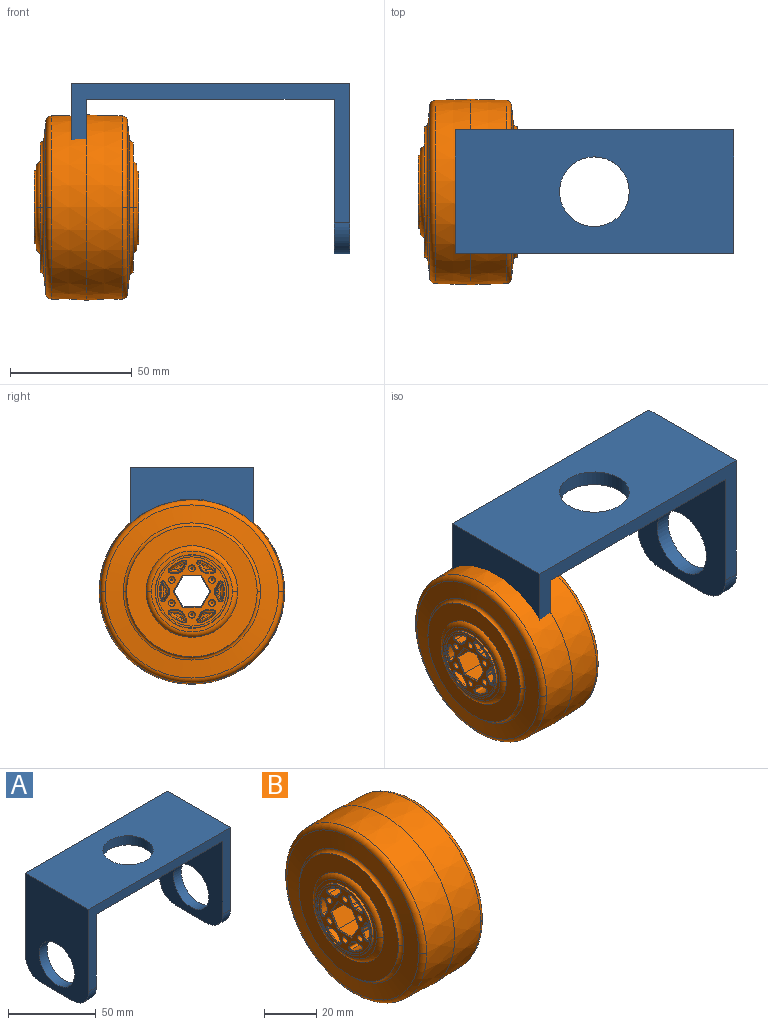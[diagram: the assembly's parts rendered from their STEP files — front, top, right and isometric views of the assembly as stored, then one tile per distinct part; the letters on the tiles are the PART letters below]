
ASSEMBLY  parts=2 mates=1
PART A: 17 faces, bbox 114.3x50.8x69.9 mm
  f0: plane 25.4x6.35mm, normal (0,0,-1), area 161.3mm2, adj f1,f7,f13,f15
  f1: plane 69.85x50.8mm, normal (1,0,0), area 2837.9mm2, adj f0,f2,f8,f9,f10,f13,f15
  f2: plane 114.3x50.8mm, normal (0,0,1), area 5165.1mm2, adj f1,f3,f8,f9,f16
  f3: plane 69.85x50.8mm, normal (-1,0,0), area 2837.9mm2, adj f2,f4,f8,f9,f11,f12,f14
  f4: plane 25.4x6.35mm, normal (0,0,-1), area 161.3mm2, adj f3,f5,f12,f14
  f5: plane 63.5x50.8mm, normal (1,0,0), area 2515.3mm2, adj f4,f6,f8,f9,f11,f12,f14
  f6: plane 101.6x50.8mm, normal (0,0,-1), area 4520mm2, adj f5,f7,f8,f9,f16
  f7: plane 63.5x50.8mm, normal (-1,0,0), area 2515.3mm2, adj f0,f6,f8,f9,f10,f13,f15
  f8: plane 114.3x57.15mm, normal (0,-1,0), area 1371mm2, adj f1,f2,f3,f5,f6,f7,f14,f15
  f9: plane 114.3x57.15mm, normal (0,1,0), area 1371mm2, adj f1,f2,f3,f5,f6,f7,f12,f13
  f10: cylinder r=14.29mm len=28.58mm, axis (1,0,0), area 570mm2, adj f1,f7
  f11: cylinder r=14.29mm len=28.58mm, axis (1,0,0), area 570mm2, adj f3,f5
  f12: cylinder r=12.7mm len=12.7mm, axis (1,0,0), area 126.7mm2, adj f3,f4,f5,f9
  f13: cylinder r=12.7mm len=12.7mm, axis (1,0,0), area 126.7mm2, adj f0,f1,f7,f9
  f14: cylinder r=12.7mm len=12.7mm, axis (-1,0,0), area 126.7mm2, adj f3,f4,f5,f8
  f15: cylinder r=12.7mm len=12.7mm, axis (-1,0,0), area 126.7mm2, adj f0,f1,f7,f8
  f16: cylinder r=14.29mm len=28.58mm, axis (0,0,1), area 570mm2, adj f2,f6
PART B: 338 faces, bbox 44.4x82.9x82.9 mm
  f0: torus R=35.31mm, axis (-1,0,0), area 378.6mm2, adj f38,f40,f52
  f1: torus R=35.31mm, axis (-1,0,0), area 378.6mm2, adj f39,f41,f53
  f2: torus R=28.32mm, axis (-1,0,0), area 191.5mm2, adj f40,f48,f54
  f3: torus R=28.32mm, axis (-1,0,0), area 191.5mm2, adj f41,f51,f55
  f4: torus R=16.62mm, axis (-1,0,0), area 161.8mm2, adj f49,f50,f51
  f5: torus R=16.62mm, axis (-1,0,0), area 161.8mm2, adj f46,f47,f48
  f6: cone r=14.2mm half-angle=0.5deg, axis (1,0,0), area 26.8mm2, adj f56,f57
  f7: cylinder r=1.38mm len=18.65mm, axis (1,0,0), area 161.1mm2, adj f14,f57
  f8: cylinder r=1.38mm len=18.65mm, axis (1,0,0), area 161.1mm2, adj f15,f57
  f9: cylinder r=1.38mm len=18.65mm, axis (1,0,0), area 161.1mm2, adj f16,f57
  f10: cylinder r=1.38mm len=18.65mm, axis (1,0,0), area 161.1mm2, adj f17,f57
  f11: cylinder r=1.38mm len=18.65mm, axis (1,0,0), area 161.1mm2, adj f18,f57
  f12: cylinder r=1.38mm len=18.65mm, axis (1,0,0), area 161.1mm2, adj f19,f57
  f13: cone r=13.01mm half-angle=1.5deg, axis (1,0,0), area 128.2mm2, adj f59,f112,f113,f147
  f14: torus R=0.38mm, axis (1,0,0), area 10mm2, adj f7,f177
  f15: torus R=0.38mm, axis (1,0,0), area 10mm2, adj f8,f178
  f16: torus R=0.38mm, axis (1,0,0), area 10mm2, adj f9,f179
  f17: torus R=0.38mm, axis (1,0,0), area 10mm2, adj f10,f180
  f18: torus R=0.38mm, axis (1,0,0), area 10mm2, adj f11,f181
  f19: torus R=0.38mm, axis (1,0,0), area 10mm2, adj f12,f182
  f20: cone r=10.06mm half-angle=1.5deg, axis (-1,0,0), area 23.4mm2, adj f87,f163,f166,f200
  f21: cone r=14.2mm half-angle=0.5deg, axis (-1,0,0), area 26.8mm2, adj f189,f207
  f22: cylinder r=1.38mm len=18.65mm, axis (-1,0,0), area 161.1mm2, adj f29,f207
  f23: cylinder r=1.38mm len=18.65mm, axis (-1,0,0), area 161.1mm2, adj f30,f207
  f24: cylinder r=1.38mm len=18.65mm, axis (-1,0,0), area 161.1mm2, adj f31,f207
  f25: cylinder r=1.38mm len=18.65mm, axis (-1,0,0), area 161.1mm2, adj f32,f207
  f26: cylinder r=1.38mm len=18.65mm, axis (-1,0,0), area 161.1mm2, adj f33,f207
  f27: cylinder r=1.38mm len=18.65mm, axis (-1,0,0), area 161.1mm2, adj f34,f207
  f28: cone r=13.01mm half-angle=1.5deg, axis (-1,0,0), area 128.2mm2, adj f249,f281,f282,f310
  f29: torus R=0.38mm, axis (-1,0,0), area 10mm2, adj f22,f315
  f30: torus R=0.38mm, axis (-1,0,0), area 10mm2, adj f23,f316
  f31: torus R=0.38mm, axis (-1,0,0), area 10mm2, adj f24,f317
  f32: torus R=0.38mm, axis (-1,0,0), area 10mm2, adj f25,f318
  f33: torus R=0.38mm, axis (-1,0,0), area 10mm2, adj f26,f319
  f34: torus R=0.38mm, axis (-1,0,0), area 10mm2, adj f27,f320
  f35: cone r=10.06mm half-angle=1.5deg, axis (1,0,0), area 23.4mm2, adj f231,f295,f298,f327
  f36: cone r=15.17mm half-angle=0.5deg, axis (-1,0,0), area 316mm2, adj f44,f56
  f37: cone r=15.17mm half-angle=0.5deg, axis (1,0,0), area 304.2mm2, adj f45,f189
  f38: cone r=38.1mm half-angle=2deg, axis (-1,0,0), area 3465.4mm2, adj f0,f39,f52
  f39: cone r=38.1mm half-angle=2deg, axis (1,0,0), area 3465.4mm2, adj f1,f38,f53
  f40: cone r=35.55mm half-angle=84deg, axis (-1,0,0), area 1486mm2, adj f0,f2,f52,f54
  f41: cone r=35.55mm half-angle=84deg, axis (1,0,0), area 1486mm2, adj f1,f3,f53,f55
  f42: cylinder r=15.11mm len=30.21mm, axis (-1,0,0), area 230.8mm2, adj f45,f49
  f43: cylinder r=15.11mm len=30.21mm, axis (-1,0,0), area 243mm2, adj f44,f46
  f44: cone r=31.03mm half-angle=77.6deg, axis (-1,0,0), area 7.8mm2, adj f36,f43
  f45: cone r=13.82mm half-angle=79.3deg, axis (1,0,0), area 7.8mm2, adj f37,f42
  f46: plane 33.24x33.24mm, normal (1,0,0), area 150.8mm2, adj f5,f43,f47
  f47: torus R=16.62mm, axis (-1,0,0), area 161.8mm2, adj f5,f46,f48
  f48: plane 53.59x53.59mm, normal (1,0,0), area 1146mm2, adj f2,f5,f47,f54
  f49: plane 33.24x33.24mm, normal (-1,0,0), area 150.8mm2, adj f4,f42,f50
  f50: torus R=16.62mm, axis (-1,0,0), area 161.8mm2, adj f4,f49,f51
  f51: plane 53.59x53.59mm, normal (-1,0,0), area 1146mm2, adj f3,f4,f50,f55
  f52: torus R=35.31mm, axis (-1,0,0), area 378.6mm2, adj f0,f38,f40
  f53: torus R=35.31mm, axis (-1,0,0), area 378.6mm2, adj f1,f39,f41
  f54: torus R=28.32mm, axis (-1,0,0), area 191.5mm2, adj f2,f40,f48
  f55: torus R=28.32mm, axis (-1,0,0), area 191.5mm2, adj f3,f41,f51
  f56: plane 29.99x29.99mm, normal (1,0,0), area 72.9mm2, adj f6,f36
  f57: plane 28.52x28.52mm, normal (1,0,0), area 288.3mm2, adj f6,f7,f8,f9,f10,f11,f12,f58
  f58: bspline ~2.05x0.93mm, area 1mm2, adj f57,f59,f65,f112
  f59: torus R=13.31mm, axis (1,0,0), area 3.3mm2, adj f13,f57,f58,f60
  f60: bspline ~2.04x0.95mm, area 1mm2, adj f57,f59,f61,f113
  f61: cylinder r=0.3mm len=2.75mm, axis (0,0.5,0.87), area 1.4mm2, adj f57,f60,f62,f114
  f62: bspline ~0.74x0.49mm, area 0.3mm2, adj f57,f61,f63,f148
  f63: torus R=9.28mm, axis (1,0,0), area 0.6mm2, adj f57,f62,f64,f191
  f64: bspline ~0.72x0.49mm, area 0.3mm2, adj f57,f63,f65,f151
  f65: cylinder r=0.3mm len=2.75mm, axis (0,-0.5,0.87), area 1.4mm2, adj f57,f58,f64,f115
  f66: bspline ~1.72x1.42mm, area 1mm2, adj f57,f67,f73,f116
  f67: torus R=13.31mm, axis (1,0,0), area 3.3mm2, adj f57,f66,f68,f117
  f68: bspline ~1.92x1.14mm, area 1mm2, adj f57,f67,f69,f118
  f69: cylinder r=0.3mm len=3mm, axis (0,1,0), area 1.4mm2, adj f57,f68,f70,f119
  f70: bspline ~0.73x0.52mm, area 0.3mm2, adj f57,f69,f71,f153
  f71: torus R=9.28mm, axis (1,0,0), area 0.6mm2, adj f57,f70,f72,f194
  f72: bspline ~0.7x0.68mm, area 0.3mm2, adj f57,f71,f73,f156
  f73: cylinder r=0.3mm len=2.75mm, axis (0,0.5,0.87), area 1.4mm2, adj f57,f66,f72,f120
  f74: bspline ~1.9x1.15mm, area 1mm2, adj f57,f75,f81,f121
  f75: torus R=13.31mm, axis (1,0,0), area 3.3mm2, adj f57,f74,f76,f122
  f76: bspline ~1.69x1.45mm, area 1mm2, adj f57,f75,f77,f123
  f77: cylinder r=0.3mm len=2.75mm, axis (0,0.5,-0.87), area 1.4mm2, adj f57,f76,f78,f124
  f78: bspline ~0.7x0.68mm, area 0.3mm2, adj f57,f77,f79,f158
  f79: torus R=9.28mm, axis (1,0,0), area 0.6mm2, adj f57,f78,f80,f197
  f80: bspline ~0.73x0.51mm, area 0.3mm2, adj f57,f79,f81,f161
  f81: cylinder r=0.3mm len=3mm, axis (0,1,0), area 1.4mm2, adj f57,f74,f80,f125
  f82: bspline ~2.05x0.93mm, area 1mm2, adj f57,f83,f89,f126
  f83: torus R=13.31mm, axis (1,0,0), area 3.3mm2, adj f57,f82,f84,f127
  f84: bspline ~2.04x0.95mm, area 1mm2, adj f57,f83,f85,f128
  f85: cylinder r=0.3mm len=2.75mm, axis (0,-0.5,-0.87), area 1.4mm2, adj f57,f84,f86,f129
  f86: bspline ~0.74x0.49mm, area 0.3mm2, adj f57,f85,f87,f163
  f87: torus R=9.28mm, axis (1,0,0), area 0.6mm2, adj f20,f57,f86,f88
  f88: bspline ~0.72x0.49mm, area 0.3mm2, adj f57,f87,f89,f166
  f89: cylinder r=0.3mm len=2.75mm, axis (0,0.5,-0.87), area 1.4mm2, adj f57,f82,f88,f130
  f90: bspline ~1.72x1.42mm, area 1mm2, adj f57,f91,f97,f131
  f91: torus R=13.31mm, axis (1,0,0), area 3.3mm2, adj f57,f90,f92,f132
  f92: bspline ~1.92x1.14mm, area 1mm2, adj f57,f91,f93,f133
  f93: cylinder r=0.3mm len=3mm, axis (0,-1,0), area 1.4mm2, adj f57,f92,f94,f134
  f94: bspline ~0.73x0.52mm, area 0.3mm2, adj f57,f93,f95,f168
  f95: torus R=9.28mm, axis (1,0,0), area 0.6mm2, adj f57,f94,f96,f202
  f96: bspline ~0.7x0.68mm, area 0.3mm2, adj f57,f95,f97,f171
  f97: cylinder r=0.3mm len=2.75mm, axis (0,-0.5,-0.87), area 1.4mm2, adj f57,f90,f96,f135
  f98: bspline ~1.9x1.15mm, area 1mm2, adj f57,f99,f105,f136
  f99: torus R=13.31mm, axis (1,0,0), area 3.3mm2, adj f57,f98,f100,f137
  f100: bspline ~1.69x1.45mm, area 1mm2, adj f57,f99,f101,f138
  f101: cylinder r=0.3mm len=2.75mm, axis (0,-0.5,0.87), area 1.4mm2, adj f57,f100,f102,f139
  f102: bspline ~0.7x0.68mm, area 0.3mm2, adj f57,f101,f103,f173
  f103: torus R=9.28mm, axis (1,0,0), area 0.6mm2, adj f57,f102,f104,f205
  f104: bspline ~0.73x0.51mm, area 0.3mm2, adj f57,f103,f105,f176
  f105: cylinder r=0.3mm len=3mm, axis (0,-1,0), area 1.4mm2, adj f57,f98,f104,f140
  f106: plane 6.66x4.02mm, normal (0.71,0.61,0.35), area 3.2mm2, adj f57,f107,f111,f141
  f107: plane 7.69x0.3mm, normal (0.71,0,0.71), area 3.2mm2, adj f57,f106,f108,f142
  f108: plane 6.66x4.02mm, normal (0.71,-0.61,0.35), area 3.2mm2, adj f57,f107,f109,f143
  f109: plane 6.66x4.02mm, normal (0.71,-0.61,-0.35), area 3.2mm2, adj f57,f108,f110,f144
  f110: plane 7.69x0.3mm, normal (0.71,0,-0.71), area 3.2mm2, adj f57,f109,f111,f145
  f111: plane 6.66x4.02mm, normal (0.71,0.61,-0.35), area 3.2mm2, adj f57,f106,f110,f146
  f112: revolved ~19.11x1.39mm, area 22.6mm2, adj f13,f58,f115,f147,f150
  f113: revolved ~19.11x1.39mm, area 22.6mm2, adj f13,f60,f114,f147,f149
  f114: plane 18.67x2.84mm, normal (0.03,0.87,-0.5), area 56mm2, adj f61,f113,f148,f149
  f115: plane 18.67x2.84mm, normal (0.03,0.87,0.5), area 56mm2, adj f65,f112,f150,f151
  f116: revolved ~19.11x1.14mm, area 22.6mm2, adj f66,f117,f120,f152,f155
  f117: cone r=13.01mm half-angle=1.5deg, axis (1,0,0), area 128.2mm2, adj f67,f116,f118,f152
  f118: revolved ~19.11x1.29mm, area 22.6mm2, adj f68,f117,f119,f152,f154
  f119: plane 18.67x3mm, normal (0.03,0,-1), area 56mm2, adj f69,f118,f153,f154
  f120: plane 18.67x2.84mm, normal (0.03,0.87,-0.5), area 56mm2, adj f73,f116,f155,f156
  f121: revolved ~19.11x1.29mm, area 22.6mm2, adj f74,f122,f125,f157,f160
  f122: cone r=13.01mm half-angle=1.5deg, axis (1,0,0), area 128.2mm2, adj f75,f121,f123,f157
  f123: revolved ~19.11x1.14mm, area 22.6mm2, adj f76,f122,f124,f157,f159
  f124: plane 18.67x2.84mm, normal (0.03,-0.87,-0.5), area 56mm2, adj f77,f123,f158,f159
  f125: plane 18.67x3mm, normal (0.03,0,-1), area 56mm2, adj f81,f121,f160,f161
  f126: revolved ~19.11x1.39mm, area 22.6mm2, adj f82,f127,f130,f162,f165
  f127: cone r=13.01mm half-angle=1.5deg, axis (1,0,0), area 128.2mm2, adj f83,f126,f128,f162
  f128: revolved ~19.11x1.39mm, area 22.6mm2, adj f84,f127,f129,f162,f164
  f129: plane 18.67x2.84mm, normal (0.03,-0.87,0.5), area 56mm2, adj f85,f128,f163,f164
  f130: plane 18.67x2.84mm, normal (0.03,-0.87,-0.5), area 56mm2, adj f89,f126,f165,f166
  f131: revolved ~19.11x1.14mm, area 22.6mm2, adj f90,f132,f135,f167,f170
  f132: cone r=13.01mm half-angle=1.5deg, axis (1,0,0), area 128.2mm2, adj f91,f131,f133,f167
  f133: revolved ~19.11x1.29mm, area 22.6mm2, adj f92,f132,f134,f167,f169
  f134: plane 18.67x3mm, normal (0.03,0,1), area 56mm2, adj f93,f133,f168,f169
  f135: plane 18.67x2.84mm, normal (0.03,-0.87,0.5), area 56mm2, adj f97,f131,f170,f171
  f136: revolved ~19.11x1.29mm, area 22.6mm2, adj f98,f137,f140,f172,f175
  f137: cone r=13.01mm half-angle=1.5deg, axis (1,0,0), area 128.2mm2, adj f99,f136,f138,f172
  f138: revolved ~19.11x1.14mm, area 22.6mm2, adj f100,f137,f139,f172,f174
  f139: plane 18.67x2.84mm, normal (0.03,0.87,0.5), area 56mm2, adj f101,f138,f173,f174
  f140: plane 18.67x3mm, normal (0.03,0,1), area 56mm2, adj f105,f136,f175,f176
  f141: plane 41.69x6.36mm, normal (0,0.87,0.5), area 306.3mm2, adj f106,f142,f146,f183
  f142: plane 41.69x7.35mm, normal (0,0,1), area 306.3mm2, adj f107,f141,f143,f184
  f143: plane 41.69x6.36mm, normal (0,-0.87,0.5), area 306.3mm2, adj f108,f142,f144,f185
  f144: plane 41.69x6.36mm, normal (0,-0.87,-0.5), area 306.3mm2, adj f109,f143,f145,f186
  f145: plane 41.69x7.35mm, normal (0,0,-1), area 306.3mm2, adj f110,f144,f146,f187
  f146: plane 41.69x6.36mm, normal (0,0.87,-0.5), area 306.3mm2, adj f111,f141,f145,f188
  f147: torus R=11.82mm, axis (1,0,0), area 6.7mm2, adj f13,f112,f113,f149,f150,f190
  f148: bspline ~19.55x0.57mm, area 5.6mm2, adj f62,f114,f149,f191,f192
  f149: cylinder r=0.7mm len=3.22mm, axis (0,0.5,0.87), area 3.1mm2, adj f113,f114,f147,f148,f190,f192
  f150: cylinder r=0.7mm len=3.22mm, axis (0,-0.5,0.87), area 3.1mm2, adj f112,f115,f147,f151,f190,f192
  f151: bspline ~19.55x0.57mm, area 5.6mm2, adj f64,f115,f150,f191,f192
  f152: torus R=11.82mm, axis (1,0,0), area 6.7mm2, adj f116,f117,f118,f154,f155,f193
  f153: bspline ~19.55x0.57mm, area 5.6mm2, adj f70,f119,f154,f194,f195
  f154: cylinder r=0.7mm len=3.31mm, axis (0,1,0), area 3.1mm2, adj f118,f119,f152,f153,f193,f195
  f155: cylinder r=0.7mm len=3.22mm, axis (0,0.5,0.87), area 3.1mm2, adj f116,f120,f152,f156,f193,f195
  f156: bspline ~19.55x0.59mm, area 5.6mm2, adj f72,f120,f155,f194,f195
  f157: torus R=11.82mm, axis (1,0,0), area 6.7mm2, adj f121,f122,f123,f159,f160,f196
  f158: bspline ~19.55x0.59mm, area 5.6mm2, adj f78,f124,f159,f197,f198
  f159: cylinder r=0.7mm len=3.22mm, axis (0,0.5,-0.87), area 3.1mm2, adj f123,f124,f157,f158,f196,f198
  f160: cylinder r=0.7mm len=3.31mm, axis (0,1,0), area 3.1mm2, adj f121,f125,f157,f161,f196,f198
  f161: bspline ~19.55x0.57mm, area 5.6mm2, adj f80,f125,f160,f197,f198
  f162: torus R=11.82mm, axis (1,0,0), area 6.7mm2, adj f126,f127,f128,f164,f165,f199
  f163: bspline ~19.55x0.57mm, area 5.6mm2, adj f20,f86,f129,f164,f200
  f164: cylinder r=0.7mm len=3.22mm, axis (0,-0.5,-0.87), area 3.1mm2, adj f128,f129,f162,f163,f199,f200
  f165: cylinder r=0.7mm len=3.22mm, axis (0,0.5,-0.87), area 3.1mm2, adj f126,f130,f162,f166,f199,f200
  f166: bspline ~19.55x0.57mm, area 5.6mm2, adj f20,f88,f130,f165,f200
  f167: torus R=11.82mm, axis (1,0,0), area 6.7mm2, adj f131,f132,f133,f169,f170,f201
  f168: bspline ~19.55x0.57mm, area 5.6mm2, adj f94,f134,f169,f202,f203
  f169: cylinder r=0.7mm len=3.31mm, axis (0,-1,0), area 3.1mm2, adj f133,f134,f167,f168,f201,f203
  f170: cylinder r=0.7mm len=3.22mm, axis (0,-0.5,-0.87), area 3.1mm2, adj f131,f135,f167,f171,f201,f203
  f171: bspline ~19.55x0.59mm, area 5.6mm2, adj f96,f135,f170,f202,f203
  f172: torus R=11.82mm, axis (1,0,0), area 6.7mm2, adj f136,f137,f138,f174,f175,f204
  f173: bspline ~19.55x0.59mm, area 5.6mm2, adj f102,f139,f174,f205,f206
  f174: cylinder r=0.7mm len=3.22mm, axis (0,-0.5,0.87), area 3.1mm2, adj f138,f139,f172,f173,f204,f206
  f175: cylinder r=0.7mm len=3.31mm, axis (0,-1,0), area 3.1mm2, adj f136,f140,f172,f176,f204,f206
  f176: bspline ~19.55x0.57mm, area 5.6mm2, adj f104,f140,f175,f205,f206
  f177: plane 0.75x0.75mm, normal (1,0,0), area 0.4mm2, adj f14
  f178: plane 0.75x0.75mm, normal (1,0,0), area 0.4mm2, adj f15
  f179: plane 0.75x0.75mm, normal (1,0,0), area 0.4mm2, adj f16
  f180: plane 0.75x0.75mm, normal (1,0,0), area 0.4mm2, adj f17
  f181: plane 0.75x0.75mm, normal (1,0,0), area 0.4mm2, adj f18
  f182: plane 0.75x0.75mm, normal (1,0,0), area 0.4mm2, adj f19
  f183: plane 6.66x4.02mm, normal (-0.71,0.61,0.35), area 3.2mm2, adj f141,f184,f188,f207
  f184: plane 7.69x0.3mm, normal (-0.71,0,0.71), area 3.2mm2, adj f142,f183,f185,f207
  f185: plane 6.66x4.02mm, normal (-0.71,-0.61,0.35), area 3.2mm2, adj f143,f184,f186,f207
  f186: plane 6.66x4.02mm, normal (-0.71,-0.61,-0.35), area 3.2mm2, adj f144,f185,f187,f207
  f187: plane 7.69x0.3mm, normal (-0.71,0,-0.71), area 3.2mm2, adj f145,f186,f188,f207
  f188: plane 6.66x4.02mm, normal (-0.71,0.61,-0.35), area 3.2mm2, adj f146,f183,f187,f207
  f189: plane 29.99x29.99mm, normal (-1,0,0), area 72.9mm2, adj f21,f37
  f190: plane 4.17x1.07mm, normal (1,0,0), area 2.8mm2, adj f147,f149,f150,f192
  f191: cone r=10.06mm half-angle=1.5deg, axis (-1,0,0), area 23.4mm2, adj f63,f148,f151,f192
  f192: torus R=10.76mm, axis (1,0,0), area 1.4mm2, adj f148,f149,f150,f151,f190,f191
  f193: plane 3.61x2.08mm, normal (1,0,0), area 2.8mm2, adj f152,f154,f155,f195
  f194: cone r=10.06mm half-angle=1.5deg, axis (-1,0,0), area 23.4mm2, adj f71,f153,f156,f195
  f195: torus R=10.76mm, axis (1,0,0), area 1.4mm2, adj f153,f154,f155,f156,f193,f194
  f196: plane 3.61x2.08mm, normal (1,0,0), area 2.8mm2, adj f157,f159,f160,f198
  f197: cone r=10.06mm half-angle=1.5deg, axis (-1,0,0), area 23.4mm2, adj f79,f158,f161,f198
  f198: torus R=10.76mm, axis (1,0,0), area 1.4mm2, adj f158,f159,f160,f161,f196,f197
  f199: plane 4.17x1.07mm, normal (1,0,0), area 2.8mm2, adj f162,f164,f165,f200
  f200: torus R=10.76mm, axis (1,0,0), area 1.4mm2, adj f20,f163,f164,f165,f166,f199
  f201: plane 3.61x2.08mm, normal (1,0,0), area 2.8mm2, adj f167,f169,f170,f203
  f202: cone r=10.06mm half-angle=1.5deg, axis (-1,0,0), area 23.4mm2, adj f95,f168,f171,f203
  f203: torus R=10.76mm, axis (1,0,0), area 1.4mm2, adj f168,f169,f170,f171,f201,f202
  f204: plane 3.61x2.08mm, normal (1,0,0), area 2.8mm2, adj f172,f174,f175,f206
  f205: cone r=10.06mm half-angle=1.5deg, axis (-1,0,0), area 23.4mm2, adj f103,f173,f176,f206
  f206: torus R=10.76mm, axis (1,0,0), area 1.4mm2, adj f173,f174,f175,f176,f204,f205
  f207: plane 28.49x28.49mm, normal (-1,0,0), area 288.3mm2, adj f21,f22,f23,f24,f25,f26,f27,f183
  f208: bspline ~0.68x0.68mm, area 0.3mm2, adj f207,f209,f215,f285
  f209: cylinder r=0.3mm len=2.75mm, axis (0,-0.5,0.87), area 1.4mm2, adj f207,f208,f210,f256
  f210: bspline ~1.72x1.42mm, area 1.1mm2, adj f207,f209,f211,f257
  f211: torus R=13.31mm, axis (-1,0,0), area 3.3mm2, adj f207,f210,f212,f258
  f212: bspline ~1.92x1.15mm, area 1.1mm2, adj f207,f211,f213,f259
  f213: cylinder r=0.3mm len=3mm, axis (0,-1,0), area 1.4mm2, adj f207,f212,f214,f260
  f214: bspline ~0.69x0.51mm, area 0.3mm2, adj f207,f213,f215,f288
  f215: torus R=9.28mm, axis (-1,0,0), area 0.6mm2, adj f207,f208,f214,f321
  f216: bspline ~0.71x0.52mm, area 0.3mm2, adj f207,f217,f223,f290
  f217: cylinder r=0.3mm len=3mm, axis (0,-1,0), area 1.4mm2, adj f207,f216,f218,f261
  f218: bspline ~1.91x1.18mm, area 1.1mm2, adj f207,f217,f219,f262
  f219: torus R=13.31mm, axis (-1,0,0), area 3.3mm2, adj f207,f218,f220,f263
  f220: bspline ~1.69x1.45mm, area 1.1mm2, adj f207,f219,f221,f264
  f221: cylinder r=0.3mm len=2.75mm, axis (0,-0.5,-0.87), area 1.4mm2, adj f207,f220,f222,f265
  f222: bspline ~0.7x0.68mm, area 0.3mm2, adj f207,f221,f223,f293
  f223: torus R=9.28mm, axis (-1,0,0), area 0.6mm2, adj f207,f216,f222,f324
  f224: bspline ~0.72x0.49mm, area 0.3mm2, adj f207,f225,f231,f295
  f225: cylinder r=0.3mm len=2.75mm, axis (0,-0.5,-0.87), area 1.4mm2, adj f207,f224,f226,f266
  f226: bspline ~2.06x0.94mm, area 1.1mm2, adj f207,f225,f227,f267
  f227: torus R=13.31mm, axis (-1,0,0), area 3.3mm2, adj f207,f226,f228,f268
  f228: bspline ~2.05x0.95mm, area 1.1mm2, adj f207,f227,f229,f269
  f229: cylinder r=0.3mm len=2.75mm, axis (0,0.5,-0.87), area 1.4mm2, adj f207,f228,f230,f270
  f230: bspline ~0.7x0.48mm, area 0.3mm2, adj f207,f229,f231,f298
  f231: torus R=9.28mm, axis (-1,0,0), area 0.6mm2, adj f35,f207,f224,f230
  f232: bspline ~0.69x0.51mm, area 0.3mm2, adj f207,f233,f239,f303
  f233: torus R=9.28mm, axis (-1,0,0), area 0.6mm2, adj f207,f232,f234,f329
  f234: bspline ~0.68x0.68mm, area 0.3mm2, adj f207,f233,f235,f300
  f235: cylinder r=0.3mm len=2.75mm, axis (0,0.5,-0.87), area 1.4mm2, adj f207,f234,f236,f271
  f236: bspline ~1.72x1.42mm, area 1.1mm2, adj f207,f235,f237,f272
  f237: torus R=13.31mm, axis (-1,0,0), area 3.3mm2, adj f207,f236,f238,f273
  f238: bspline ~1.92x1.15mm, area 1.1mm2, adj f207,f237,f239,f274
  f239: cylinder r=0.3mm len=3mm, axis (0,1,0), area 1.4mm2, adj f207,f232,f238,f275
  f240: bspline ~0.71x0.52mm, area 0.3mm2, adj f207,f241,f247,f305
  f241: cylinder r=0.3mm len=3mm, axis (0,1,0), area 1.4mm2, adj f207,f240,f242,f276
  f242: bspline ~1.91x1.18mm, area 1.1mm2, adj f207,f241,f243,f277
  f243: torus R=13.31mm, axis (-1,0,0), area 3.3mm2, adj f207,f242,f244,f278
  f244: bspline ~1.69x1.45mm, area 1.1mm2, adj f207,f243,f245,f279
  f245: cylinder r=0.3mm len=2.75mm, axis (0,0.5,0.87), area 1.4mm2, adj f207,f244,f246,f280
  f246: bspline ~0.7x0.68mm, area 0.3mm2, adj f207,f245,f247,f308
  f247: torus R=9.28mm, axis (-1,0,0), area 0.6mm2, adj f207,f240,f246,f332
  f248: bspline ~2.06x0.94mm, area 1.1mm2, adj f207,f249,f255,f281
  f249: torus R=13.31mm, axis (-1,0,0), area 3.3mm2, adj f28,f207,f248,f250
  f250: bspline ~2.05x0.95mm, area 1.1mm2, adj f207,f249,f251,f282
  f251: cylinder r=0.3mm len=2.75mm, axis (0,-0.5,0.87), area 1.4mm2, adj f207,f250,f252,f283
  f252: bspline ~0.7x0.48mm, area 0.3mm2, adj f207,f251,f253,f311
  f253: torus R=9.28mm, axis (-1,0,0), area 0.6mm2, adj f207,f252,f254,f337
  f254: bspline ~0.72x0.49mm, area 0.3mm2, adj f207,f253,f255,f313
  f255: cylinder r=0.3mm len=2.75mm, axis (0,0.5,0.87), area 1.4mm2, adj f207,f248,f254,f284
  f256: plane 18.67x2.84mm, normal (-0.03,-0.87,-0.5), area 56mm2, adj f209,f257,f285,f286
  f257: revolved ~19.11x1.13mm, area 22.6mm2, adj f210,f256,f258,f286,f287
  f258: cone r=13.01mm half-angle=1.5deg, axis (-1,0,0), area 128.2mm2, adj f211,f257,f259,f287
  f259: revolved ~19.11x1.51mm, area 52.8mm2, adj f212,f258,f260,f287,f289
  f260: plane 20.17x4.5mm, normal (-0.03,0,-1), area 56mm2, adj f213,f259,f288,f289
  f261: plane 18.67x3mm, normal (-0.03,0,-1), area 56mm2, adj f217,f262,f290,f291
  f262: revolved ~19.11x1.29mm, area 22.6mm2, adj f218,f261,f263,f291,f292
  f263: cone r=13.01mm half-angle=1.5deg, axis (-1,0,0), area 128.2mm2, adj f219,f262,f264,f292
  f264: revolved ~19.11x1.51mm, area 52.8mm2, adj f220,f263,f265,f292,f294
  f265: plane 20.17x4.34mm, normal (-0.03,0.87,-0.5), area 56mm2, adj f221,f264,f293,f294
  f266: plane 18.67x2.84mm, normal (-0.03,0.87,-0.5), area 56mm2, adj f225,f267,f295,f296
  f267: revolved ~19.11x1.38mm, area 22.6mm2, adj f226,f266,f268,f296,f297
  f268: cone r=13.01mm half-angle=1.5deg, axis (-1,0,0), area 128.2mm2, adj f227,f267,f269,f297
  f269: revolved ~19.11x1.51mm, area 52.8mm2, adj f228,f268,f270,f297,f299
  f270: plane 20.17x4.34mm, normal (-0.03,0.87,0.5), area 56mm2, adj f229,f269,f298,f299
  f271: plane 18.67x2.84mm, normal (-0.03,0.87,0.5), area 56mm2, adj f235,f272,f300,f301
  f272: revolved ~19.11x1.13mm, area 22.6mm2, adj f236,f271,f273,f301,f302
  f273: cone r=13.01mm half-angle=1.5deg, axis (-1,0,0), area 128.2mm2, adj f237,f272,f274,f302
  f274: revolved ~19.11x1.51mm, area 52.8mm2, adj f238,f273,f275,f302,f304
  f275: plane 20.17x4.5mm, normal (-0.03,0,1), area 56mm2, adj f239,f274,f303,f304
  f276: plane 18.67x3mm, normal (-0.03,0,1), area 56mm2, adj f241,f277,f305,f306
  f277: revolved ~19.11x1.29mm, area 22.6mm2, adj f242,f276,f278,f306,f307
  f278: cone r=13.01mm half-angle=1.5deg, axis (-1,0,0), area 128.2mm2, adj f243,f277,f279,f307
  f279: revolved ~19.11x1.51mm, area 52.8mm2, adj f244,f278,f280,f307,f309
  f280: plane 20.17x4.34mm, normal (-0.03,-0.87,0.5), area 56mm2, adj f245,f279,f308,f309
  f281: revolved ~19.11x1.38mm, area 22.6mm2, adj f28,f248,f284,f310,f314
  f282: revolved ~19.11x1.51mm, area 52.8mm2, adj f28,f250,f283,f310,f312
  f283: plane 20.17x4.34mm, normal (-0.03,-0.87,-0.5), area 56mm2, adj f251,f282,f311,f312
  f284: plane 18.67x2.84mm, normal (-0.03,-0.87,0.5), area 56mm2, adj f255,f281,f313,f314
  f285: bspline ~19.55x0.59mm, area 5.6mm2, adj f208,f256,f286,f321,f322
  f286: cylinder r=0.7mm len=3.22mm, axis (0,-0.5,0.87), area 3.1mm2, adj f256,f257,f285,f287,f322,f323
  f287: torus R=11.82mm, axis (-1,0,0), area 6.7mm2, adj f257,f258,f259,f286,f289,f323
  f288: bspline ~19.55x0.57mm, area 5.6mm2, adj f214,f260,f289,f321,f322
  f289: cylinder r=0.7mm len=3.31mm, axis (0,-1,0), area 3.1mm2, adj f259,f260,f287,f288,f322,f323
  f290: bspline ~19.55x0.57mm, area 5.6mm2, adj f216,f261,f291,f324,f325
  f291: cylinder r=0.7mm len=3.31mm, axis (0,-1,0), area 3.1mm2, adj f261,f262,f290,f292,f325,f326
  f292: torus R=11.82mm, axis (-1,0,0), area 6.7mm2, adj f262,f263,f264,f291,f294,f326
  f293: bspline ~19.55x0.59mm, area 5.6mm2, adj f222,f265,f294,f324,f325
  f294: cylinder r=0.7mm len=3.22mm, axis (0,-0.5,-0.87), area 3.1mm2, adj f264,f265,f292,f293,f325,f326
  f295: bspline ~19.55x0.57mm, area 5.6mm2, adj f35,f224,f266,f296,f327
  f296: cylinder r=0.7mm len=3.22mm, axis (0,-0.5,-0.87), area 3.1mm2, adj f266,f267,f295,f297,f327,f328
  f297: torus R=11.82mm, axis (-1,0,0), area 6.7mm2, adj f267,f268,f269,f296,f299,f328
  f298: bspline ~19.55x0.57mm, area 5.6mm2, adj f35,f230,f270,f299,f327
  f299: cylinder r=0.7mm len=3.22mm, axis (0,0.5,-0.87), area 3.1mm2, adj f269,f270,f297,f298,f327,f328
  f300: bspline ~19.55x0.59mm, area 5.6mm2, adj f234,f271,f301,f329,f330
  f301: cylinder r=0.7mm len=3.22mm, axis (0,0.5,-0.87), area 3.1mm2, adj f271,f272,f300,f302,f330,f331
  f302: torus R=11.82mm, axis (-1,0,0), area 6.7mm2, adj f272,f273,f274,f301,f304,f331
  f303: bspline ~19.55x0.57mm, area 5.6mm2, adj f232,f275,f304,f329,f330
  f304: cylinder r=0.7mm len=3.31mm, axis (0,1,0), area 3.1mm2, adj f274,f275,f302,f303,f330,f331
  f305: bspline ~19.55x0.57mm, area 5.6mm2, adj f240,f276,f306,f332,f333
  f306: cylinder r=0.7mm len=3.31mm, axis (0,1,0), area 3.1mm2, adj f276,f277,f305,f307,f333,f334
  f307: torus R=11.82mm, axis (-1,0,0), area 6.7mm2, adj f277,f278,f279,f306,f309,f334
  f308: bspline ~19.55x0.59mm, area 5.6mm2, adj f246,f280,f309,f332,f333
  f309: cylinder r=0.7mm len=3.22mm, axis (0,0.5,0.87), area 3.1mm2, adj f279,f280,f307,f308,f333,f334
  f310: torus R=11.82mm, axis (-1,0,0), area 6.7mm2, adj f28,f281,f282,f312,f314,f335
  f311: bspline ~19.55x0.57mm, area 5.6mm2, adj f252,f283,f312,f336,f337
  f312: cylinder r=0.7mm len=3.22mm, axis (0,-0.5,0.87), area 3.1mm2, adj f282,f283,f310,f311,f335,f336
  f313: bspline ~19.55x0.57mm, area 5.6mm2, adj f254,f284,f314,f336,f337
  f314: cylinder r=0.7mm len=3.22mm, axis (0,0.5,0.87), area 3.1mm2, adj f281,f284,f310,f313,f335,f336
  f315: plane 0.75x0.75mm, normal (-1,0,0), area 0.4mm2, adj f29
  f316: plane 0.75x0.75mm, normal (-1,0,0), area 0.4mm2, adj f30
  f317: plane 0.75x0.75mm, normal (-1,0,0), area 0.4mm2, adj f31
  f318: plane 0.75x0.75mm, normal (-1,0,0), area 0.4mm2, adj f32
  f319: plane 0.75x0.75mm, normal (-1,0,0), area 0.4mm2, adj f33
  f320: plane 0.75x0.75mm, normal (-1,0,0), area 0.4mm2, adj f34
  f321: cone r=10.06mm half-angle=1.5deg, axis (1,0,0), area 23.4mm2, adj f215,f285,f288,f322
  f322: torus R=10.76mm, axis (-1,0,0), area 1.4mm2, adj f285,f286,f288,f289,f321,f323
  f323: plane 3.61x2.08mm, normal (-1,0,0), area 2.8mm2, adj f286,f287,f289,f322
  f324: cone r=10.06mm half-angle=1.5deg, axis (1,0,0), area 23.4mm2, adj f223,f290,f293,f325
  f325: torus R=10.76mm, axis (-1,0,0), area 1.4mm2, adj f290,f291,f293,f294,f324,f326
  f326: plane 3.61x2.08mm, normal (-1,0,0), area 2.8mm2, adj f291,f292,f294,f325
  f327: torus R=10.76mm, axis (-1,0,0), area 1.4mm2, adj f35,f295,f296,f298,f299,f328
  f328: plane 4.17x1.07mm, normal (-1,0,0), area 2.8mm2, adj f296,f297,f299,f327
  f329: cone r=10.06mm half-angle=1.5deg, axis (1,0,0), area 23.4mm2, adj f233,f300,f303,f330
  f330: torus R=10.76mm, axis (-1,0,0), area 1.4mm2, adj f300,f301,f303,f304,f329,f331
  f331: plane 3.61x2.08mm, normal (-1,0,0), area 2.8mm2, adj f301,f302,f304,f330
  f332: cone r=10.06mm half-angle=1.5deg, axis (1,0,0), area 23.4mm2, adj f247,f305,f308,f333
  f333: torus R=10.76mm, axis (-1,0,0), area 1.4mm2, adj f305,f306,f308,f309,f332,f334
  f334: plane 3.61x2.08mm, normal (-1,0,0), area 2.8mm2, adj f306,f307,f309,f333
  f335: plane 4.17x1.07mm, normal (-1,0,0), area 2.8mm2, adj f310,f312,f314,f336
  f336: torus R=10.76mm, axis (-1,0,0), area 1.4mm2, adj f311,f312,f313,f314,f335,f337
  f337: cone r=10.06mm half-angle=1.5deg, axis (1,0,0), area 23.4mm2, adj f253,f311,f313,f336
PLACE A t=(4.84,-18.91,-9.6)mm fixed
PLACE B t=(-45.96,-44.31,-9.6)mm
MATE cylindrical A.f10 <-> B.f6  axis (1,0,0) through (-45.96,-44.31,-9.6)mm
